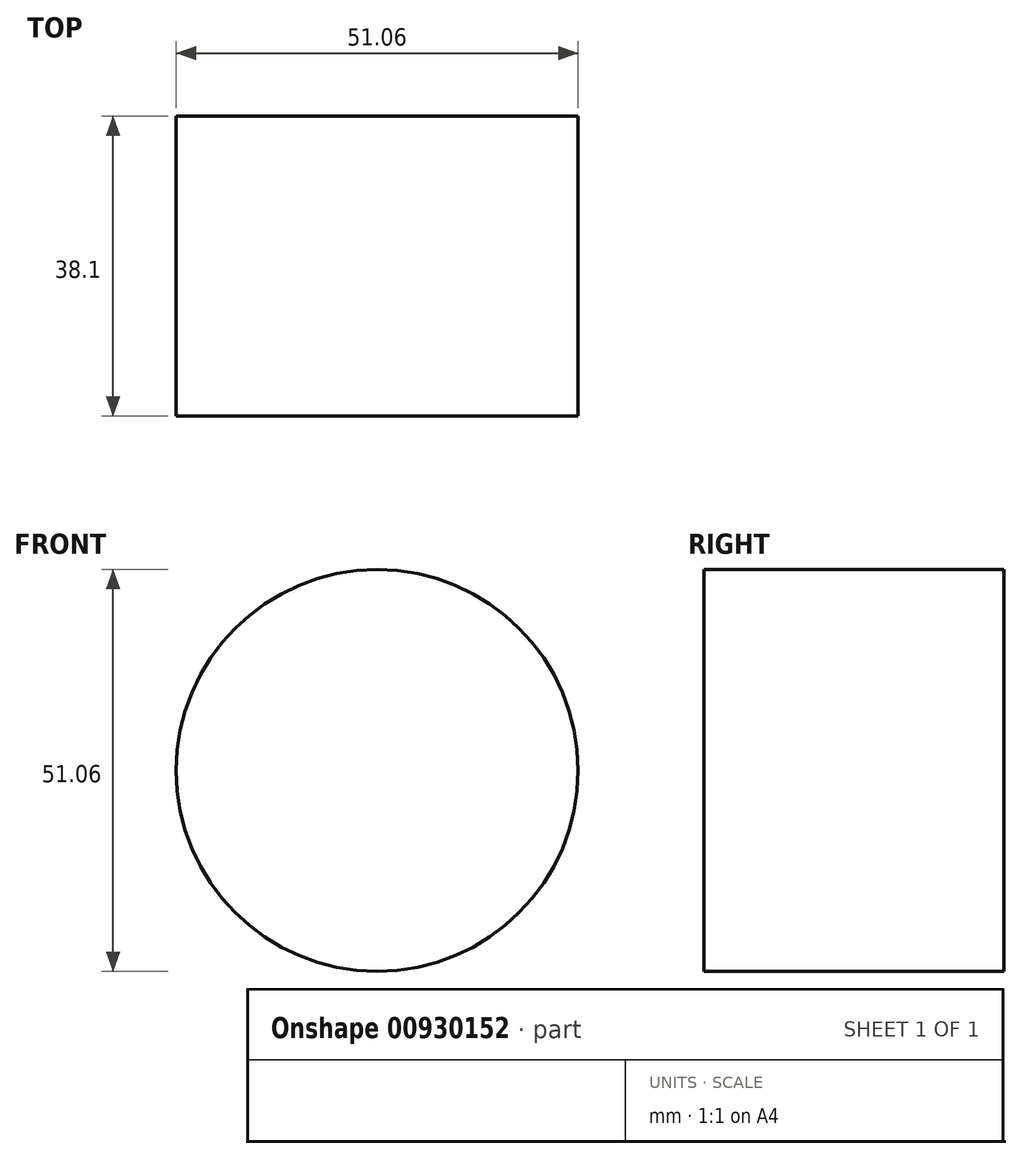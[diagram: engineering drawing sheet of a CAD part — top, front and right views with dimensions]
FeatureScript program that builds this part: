
annotation { "Feature Type Name" : "Feature", "Feature Type Description" : "" }
export const myFeature = defineFeature(function(context is Context, id is Id, definition is map)
    precondition{}
    {
        {
            var Q0;
            Q0=qCreatedBy(makeId("Front.planeOp"),FACE);
            var sketch = newSketch(context, id + "F0", { "sketchPlane" : qUnion([Q0])});
            skCircle(sketch, "E0", {"center": v(0, 0) * mm, "radius": 25.53 * mm});
            skSolve(sketch);
        }
        {
            var Q0;
            Q0=makeQuery(id+"F0.imprint","IMPRINT",FACE,{"disambiguationData":[TD([[makeQuery(id+"F0.imprint","IMPRINT",EDGE,{"derivedFrom":sQuery(id+"F0.wireOp",EDGE,"E0")}),1.0]])]});
            extrude(context, id + "F1", {"entities" : qUnion([Q0]), "depth" : 38.1 * mm, "offsetDistance" : 25.4 * mm});
        }
    });
